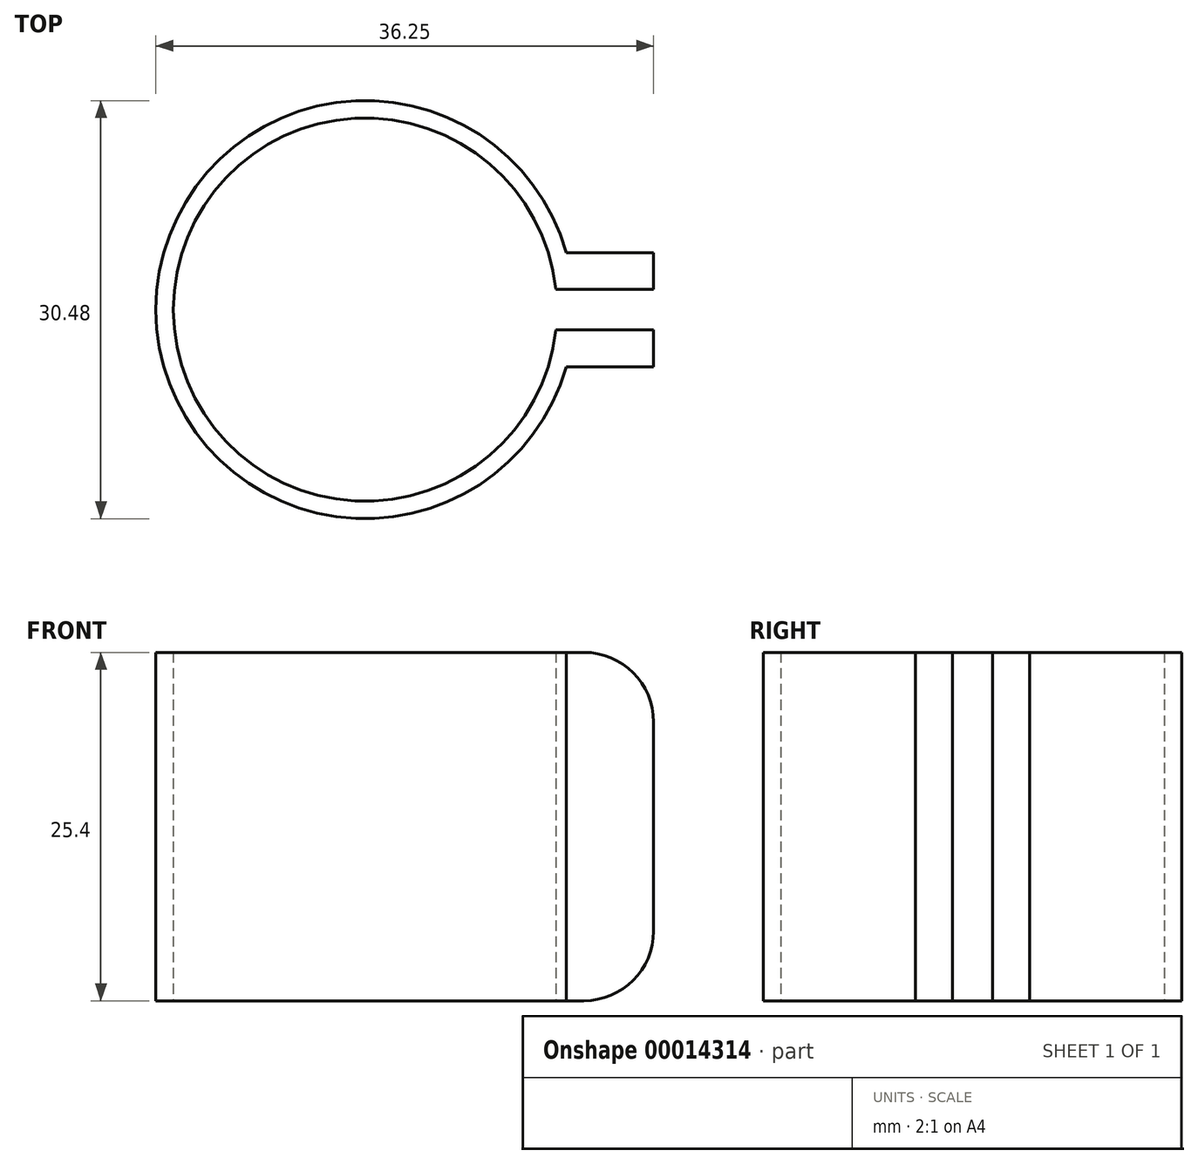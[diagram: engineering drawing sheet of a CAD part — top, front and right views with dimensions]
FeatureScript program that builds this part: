
annotation { "Feature Type Name" : "Feature", "Feature Type Description" : "" }
export const myFeature = defineFeature(function(context is Context, id is Id, definition is map)
    precondition{}
    {
        {
            var Q0;
            Q0=qCreatedBy(makeId("Top.planeOp"),FACE);
            var sketch = newSketch(context, id + "F0", { "sketchPlane" : qUnion([Q0])});
            skCircle(sketch, "E0", {"center": v(0, 0) * mm, "radius": 13.97 * mm});
            skCircle(sketch, "E1", {"center": v(0, 0) * mm, "radius": 15.24 * mm});
            skPoint(sketch, "E2.rect.middle", {"position": v(13.97, 0) * mm});
            skLineSegment(sketch, "E3", {"start": v(14.66, -4.16) * mm, "end": v(21.01, -4.16) * mm});
            skLineSegment(sketch, "E4", {"start": v(21.01, -1.47) * mm, "end": v(13.9, -1.47) * mm});
            skLineSegment(sketch, "E5", {"start": v(13.9, 1.47) * mm, "end": v(21.01, 1.47) * mm});
            skLineSegment(sketch, "E6", {"start": v(21.01, 4.16) * mm, "end": v(21.01, 1.47) * mm});
            skLineSegment(sketch, "E7", {"start": v(21.01, -1.47) * mm, "end": v(21.01, -4.16) * mm});
            skLineSegment(sketch, "E8", {"start": v(21.01, 4.16) * mm, "end": v(14.66, 4.16) * mm});
            skSolve(sketch);
        }
        {
            var Q0;
            {var subQ3=sQuery(id+"F0.wireOp",EDGE,"E0");var subQ5=sQuery(id+"F0.wireOp",EDGE,"E4");var subQ7=makeQuery(id+"F0.imprint","INTERSECT",VERTEX,{"derivedFrom":[subQ3,subQ5]});Q0=makeQuery(id+"F0.imprint","IMPRINT",FACE,{"disambiguationData":[TD([[makeQuery(id+"F0.imprint","IMPRINT",EDGE,{"disambiguationData":[TD([[subQ7,1.0]])],"derivedFrom":subQ3}),-1.0]])]});}
            var Q1;
            {var subQ1=sQuery(id+"F0.wireOp",EDGE,"E6");Q1=makeQuery(id+"F0.imprint","IMPRINT",FACE,{"disambiguationData":[TD([[makeQuery(id+"F0.imprint","IMPRINT",EDGE,{"derivedFrom":subQ1}),-1.0]])]});}
            var Q2;
            {var subQ4=sQuery(id+"F0.wireOp",EDGE,"E3");Q2=makeQuery(id+"F0.imprint","IMPRINT",FACE,{"disambiguationData":[TD([[makeQuery(id+"F0.imprint","IMPRINT",EDGE,{"derivedFrom":subQ4}),1.0]])]});}
            extrude(context, id + "F1", {"entities" : qUnion([Q0, Q1, Q2]), "depth" : 25.4 * mm});
        }
        {
            var Q0;
            Q0=makeQuery(id+"F1.opExtrude","CAP_EDGE",EDGE,{"disambiguationData":[OSD([sQuery(id+"F0.wireOp",EDGE,"E7")])],"isStart":false});
            var Q1;
            Q1=makeQuery(id+"F1.opExtrude","CAP_EDGE",EDGE,{"disambiguationData":[OSD([sQuery(id+"F0.wireOp",EDGE,"E6")])],"isStart":false});
            var Q2;
            Q2=makeQuery(id+"F1.opExtrude","CAP_EDGE",EDGE,{"disambiguationData":[OSD([sQuery(id+"F0.wireOp",EDGE,"E7")])],"isStart":true});
            var Q3;
            Q3=makeQuery(id+"F1.opExtrude","CAP_EDGE",EDGE,{"disambiguationData":[OSD([sQuery(id+"F0.wireOp",EDGE,"E6")])],"isStart":true});
            fillet(context, id + "F2", {"entities" : qUnion([Q0, Q1, Q2, Q3]), "radius" : 5.08 * mm, "tangentPropagation" : true, "allowEdgeOverflow" : false});
        }
        {
            var Q0;
            Q0=makeQuery(id+"F1.opExtrude","SWEPT_BODY",BODY,{"disambiguationData":[OSD([sQuery(id+"F0.wireOp",EDGE,"E0"),sQuery(id+"F0.wireOp",EDGE,"E1"),sQuery(id+"F0.wireOp",EDGE,"E3"),sQuery(id+"F0.wireOp",EDGE,"E4"),sQuery(id+"F0.wireOp",EDGE,"E5"),sQuery(id+"F0.wireOp",EDGE,"E6"),sQuery(id+"F0.wireOp",EDGE,"E7"),sQuery(id+"F0.wireOp",EDGE,"E8")])]});
            transform(context, id + "F3", {"entities" : qUnion([Q0]), "transformType" : TransformType.TRANSLATION_3D, "dx" : 0 * mm, "dy" : 0 * mm, "dz" : 0 * mm, "makeCopy" : true});
        }
    });
